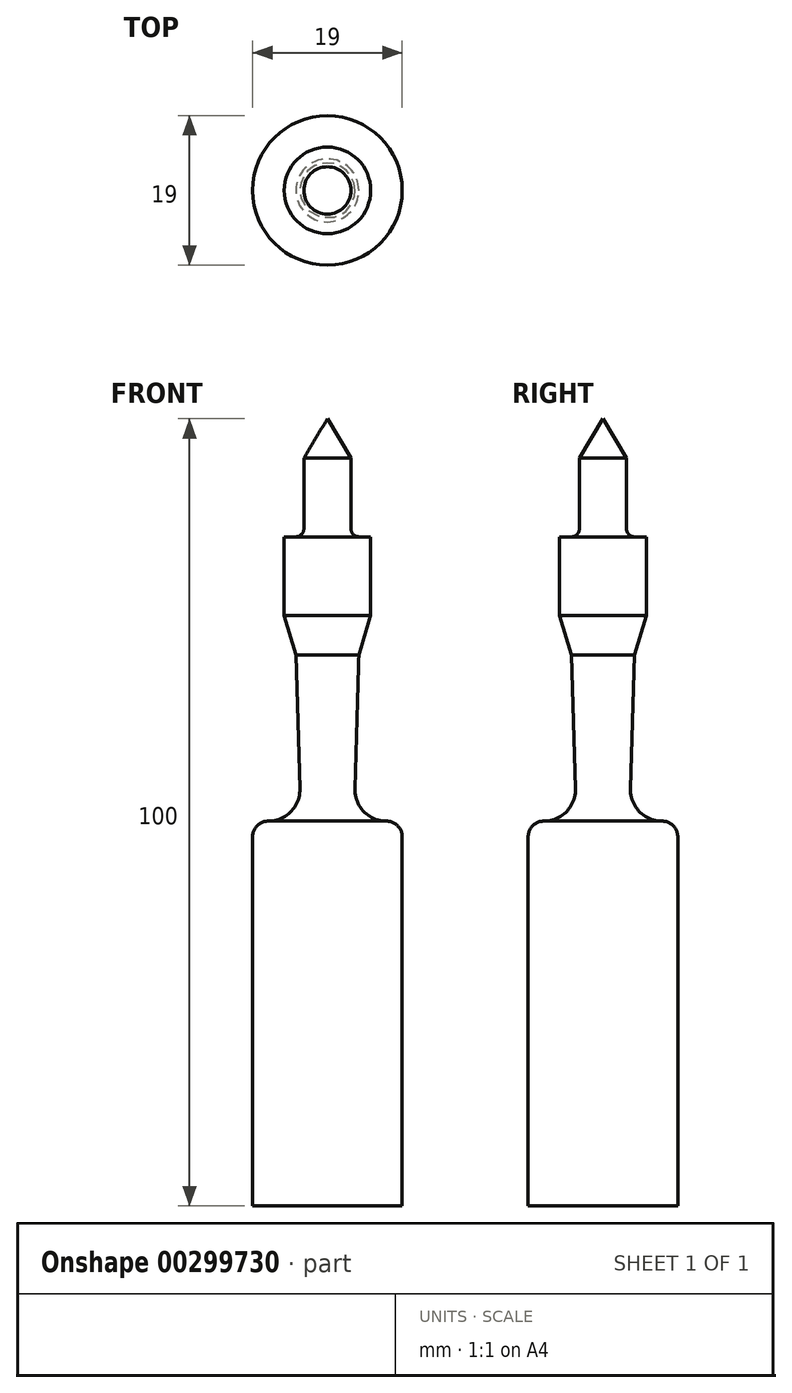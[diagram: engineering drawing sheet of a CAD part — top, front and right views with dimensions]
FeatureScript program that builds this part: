
annotation { "Feature Type Name" : "Feature", "Feature Type Description" : "" }
export const myFeature = defineFeature(function(context is Context, id is Id, definition is map)
    precondition{}
    {
        {
            var Q0;
            Q0=qCreatedBy(makeId("Front.planeOp"),FACE);
            var sketch = newSketch(context, id + "F0", { "sketchPlane" : qUnion([Q0])});
            skLineSegment(sketch, "E0", {"start": v(0, 0) * mm, "end": v(0, -100) * mm});
            skLineSegment(sketch, "E1", {"start": v(0, 0) * mm, "end": v(3, -5) * mm});
            skLineSegment(sketch, "E2", {"start": v(3, -5) * mm, "end": v(3, -14) * mm});
            skArc(sketch, "E3", {"start": v(3, -14) * mm, "mid": v(3.3, -14.7) * mm, "end": v(4, -15) * mm});
            skLineSegment(sketch, "E4", {"start": v(4, -15) * mm, "end": v(5.5, -15) * mm});
            skLineSegment(sketch, "E5", {"start": v(5.5, -15) * mm, "end": v(5.5, -25) * mm});
            skLineSegment(sketch, "E6", {"start": v(5.5, -25) * mm, "end": v(4, -30) * mm});
            skLineSegment(sketch, "E7", {"start": v(4, -30) * mm, "end": v(3.5, -47) * mm});
            skArc(sketch, "E8", {"start": v(3.5, -47) * mm, "mid": v(4.63, -49.9) * mm, "end": v(7.5, -51.12) * mm});
            skArc(sketch, "E9", {"start": v(9.5, -53.12) * mm, "mid": v(8.91, -51.7) * mm, "end": v(7.5, -51.12) * mm});
            skLineSegment(sketch, "E10", {"start": v(9.5, -53.12) * mm, "end": v(9.5, -100) * mm});
            skLineSegment(sketch, "E11", {"start": v(9.5, -100) * mm, "end": v(0, -100) * mm});
            skSolve(sketch);
        }
        {
            var Q0;
            Q0 = qSketchRegion(id + "F0", true);
            var Q1;
            Q1=sQuery(id+"F0.wireOp",EDGE,"E0");
            revolve(context, id + "F1", {"entities" : qUnion([Q0]), "axis" : qUnion([Q1]), "revolveType" : RevolveType.FULL});
        }
    });
